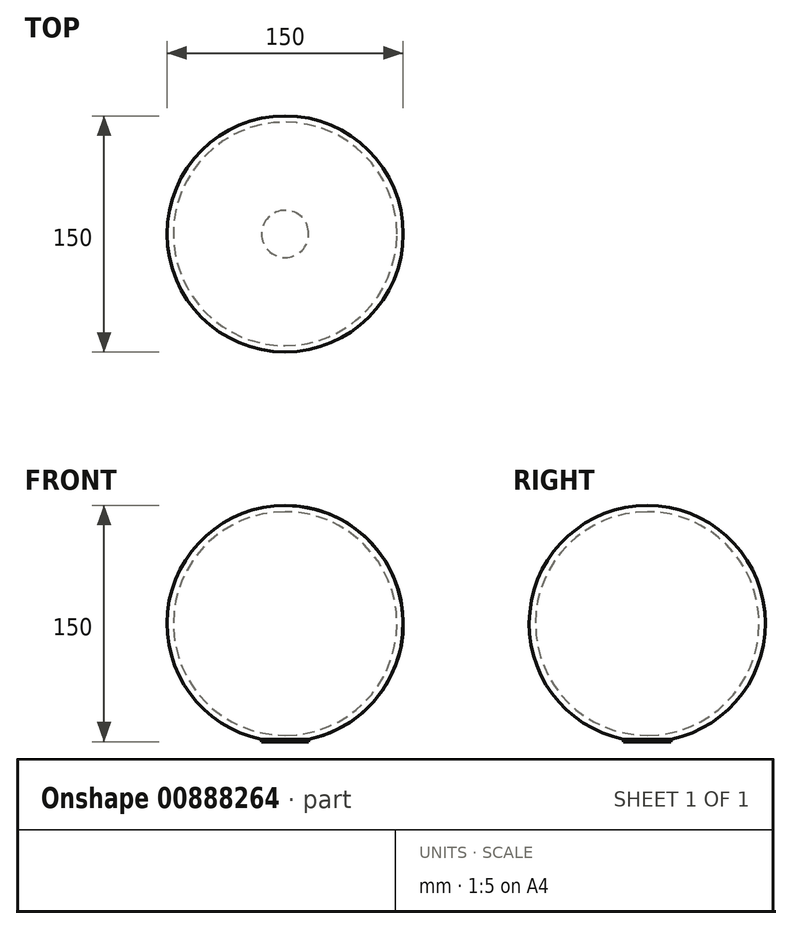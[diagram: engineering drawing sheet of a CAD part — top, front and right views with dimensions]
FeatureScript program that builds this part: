
annotation { "Feature Type Name" : "Feature", "Feature Type Description" : "" }
export const myFeature = defineFeature(function(context is Context, id is Id, definition is map)
    precondition{}
    {
        {
            var Q0;
            Q0=qCreatedBy(makeId("Front.planeOp"),FACE);
            var sketch = newSketch(context, id + "F0", { "sketchPlane" : qUnion([Q0])});
            skCircle(sketch, "E0", {"center": v(0, 75) * mm, "radius": 75 * mm});
            skLineSegment(sketch, "E1.bottom", {"start": v(0, 0) * mm, "end": v(15, 0) * mm});
            skLineSegment(sketch, "E1.top", {"start": v(0, 1.52) * mm, "end": v(15, 1.52) * mm});
            skLineSegment(sketch, "E1.left", {"start": v(0, 0) * mm, "end": v(0, 1.52) * mm});
            skLineSegment(sketch, "E1.right", {"start": v(15, 0) * mm, "end": v(15, 1.52) * mm});
            skCircle(sketch, "E2", {"center": v(0, 75) * mm, "radius": 71 * mm});
            skLineSegment(sketch, "E3", {"start": v(0, 150) * mm, "end": v(0, 0) * mm});
            skSolve(sketch);
        }
        {
            var Q0;
            {var subQ5=sQuery(id+"F0.wireOp",EDGE,"E1.top");Q0=makeQuery(id+"F0.imprint","IMPRINT",FACE,{"disambiguationData":[TD([[makeQuery(id+"F0.imprint","IMPRINT",EDGE,{"derivedFrom":subQ5}),1.0]])]});}
            var Q1;
            {var subQ3=sQuery(id+"F0.wireOp",EDGE,"E1.top");Q1=makeQuery(id+"F0.imprint","IMPRINT",FACE,{"disambiguationData":[TD([[makeQuery(id+"F0.imprint","IMPRINT",EDGE,{"derivedFrom":subQ3}),-1.0]])]});}
            var Q2;
            {var subQ0=sQuery(id+"F0.wireOp",EDGE,"E1.bottom");Q2=makeQuery(id+"F0.imprint","IMPRINT",FACE,{"disambiguationData":[TD([[makeQuery(id+"F0.imprint","IMPRINT",EDGE,{"derivedFrom":subQ0}),1.0]])]});}
            var Q3;
            Q3=sQuery(id+"F0.wireOp",EDGE,"E3");
            revolve(context, id + "F1", {"surfaceOperationType" : NewSurfaceOperationType.NEW, "entities" : qUnion([Q0, Q1, Q2]), "axis" : qUnion([Q3]), "revolveType" : RevolveType.FULL});
        }
    });
